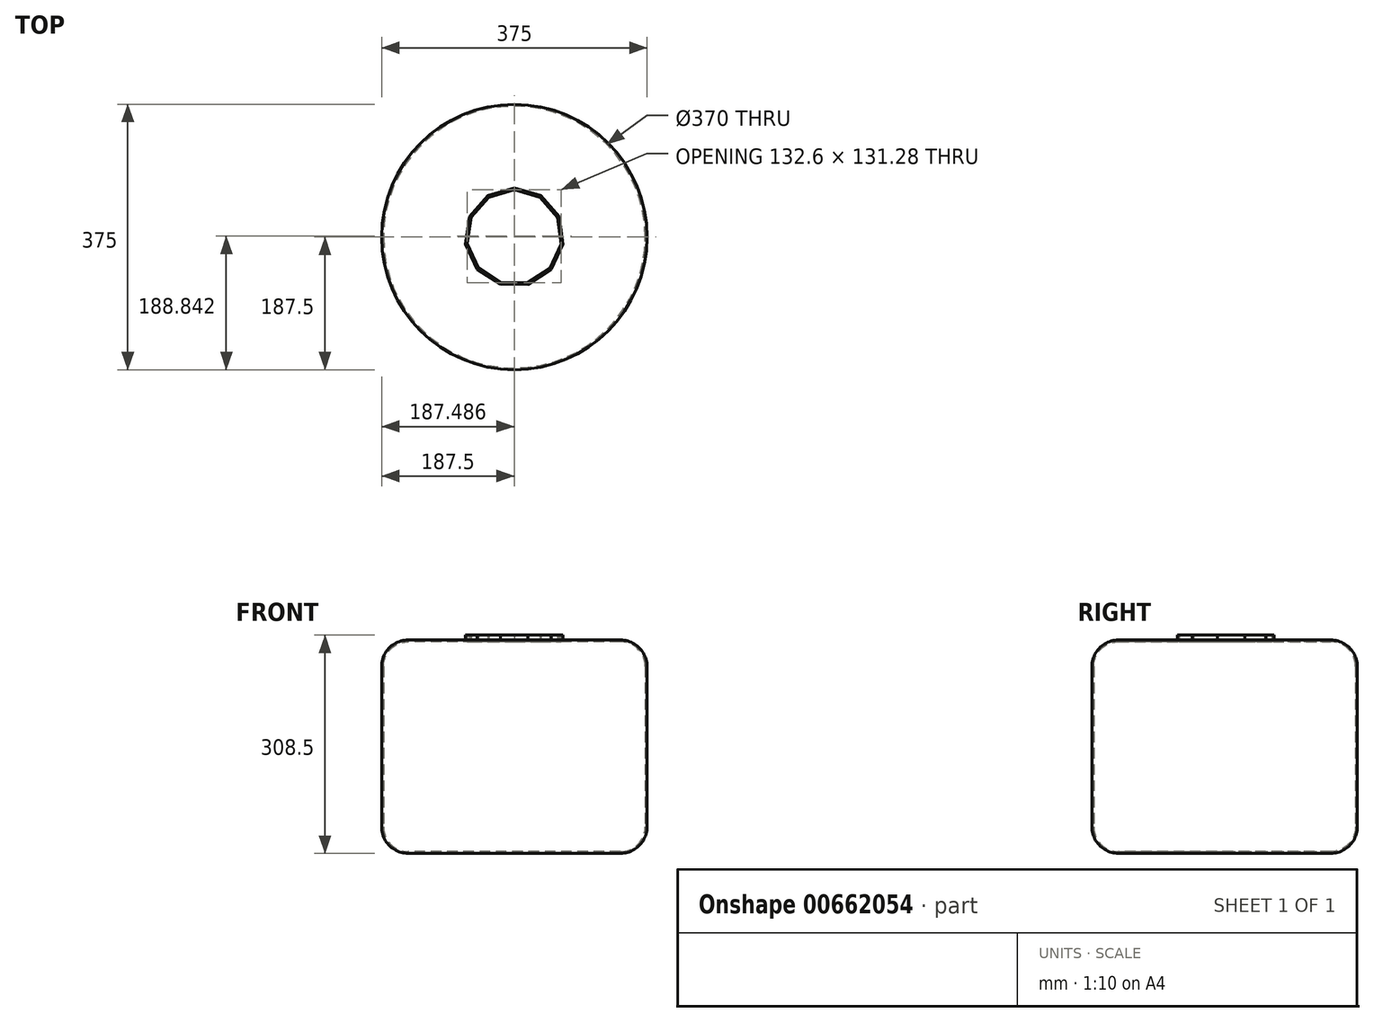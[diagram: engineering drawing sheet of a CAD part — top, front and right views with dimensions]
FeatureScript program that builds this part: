
annotation { "Feature Type Name" : "Feature", "Feature Type Description" : "" }
export const myFeature = defineFeature(function(context is Context, id is Id, definition is map)
    precondition{}
    {
        {
            var Q0;
            Q0=qCreatedBy(makeId("Top.planeOp"),FACE);
            var sketch = newSketch(context, id + "F0", { "sketchPlane" : qUnion([Q0])});
            skCircle(sketch, "E0", {"center": v(0, 0) * mm, "radius": 250 * mm});
            skSolve(sketch);
        }
        {
            var Q0;
            Q0=qSketchRegion(id+"F0",true);
            extrude(context, id + "F1", {"entities" : qUnion([Q0]), "depth" : 402 * mm, "offsetDistance" : 25 * mm});
        }
        {
            var Q0;
            Q0=makeQuery(id+"F1.opExtrude","CAP_EDGE",EDGE,{"disambiguationData":[OSD([sQuery(id+"F0.wireOp",EDGE,"E0")])],"isStart":false});
            var Q1;
            Q1=makeQuery(id+"F1.opExtrude","CAP_EDGE",EDGE,{"disambiguationData":[OSD([sQuery(id+"F0.wireOp",EDGE,"E0")])],"isStart":true});
            fillet(context, id + "F2", {"entities" : qUnion([Q0, Q1]), "radius" : 50 * mm, "tangentPropagation" : true, "allowEdgeOverflow" : false});
        }
        {
            var Q0;
            Q0=makeQuery(id+"F1.opExtrude","SWEPT_BODY",BODY,{"disambiguationData":[OSD([sQuery(id+"F0.wireOp",EDGE,"E0")])]});
            var Q1;
            Q1=qCreatedBy(makeId("Origin.pointOp"),VERTEX);
            transform(context, id + "F3", {"entities" : qUnion([Q0]), "transformType" : TransformType.SCALE_UNIFORMLY, "scale" : .75, "scalePoint" : qUnion([Q1]), "makeCopy" : false});
        }
        {
            var Q0;
            Q0=makeQuery(id+"F1.opExtrude","CAP_FACE",FACE,{"disambiguationData":[OSD([sQuery(id+"F0.wireOp",EDGE,"E0")])],"isStart":false});
            var sketch = newSketch(context, id + "F4", { "sketchPlane" : qUnion([Q0])});
            skCircle(sketch, "E1.cCircle", {"center": v(0, 0) * mm, "radius": 66.77 * mm, "construction": true});
            skLineSegment(sketch, "E1.0", {"start": v(68.86, -10) * mm, "end": v(52.52, -45.65) * mm});
            skLineSegment(sketch, "E1.1", {"start": v(52.52, -45.65) * mm, "end": v(19.5, -66.8) * mm});
            skLineSegment(sketch, "E1.2", {"start": v(19.5, -66.8) * mm, "end": v(-19.7, -66.74) * mm});
            skLineSegment(sketch, "E1.3", {"start": v(-19.7, -66.74) * mm, "end": v(-52.66, -45.49) * mm});
            skLineSegment(sketch, "E1.4", {"start": v(-52.66, -45.49) * mm, "end": v(-68.9, -9.8) * mm});
            skLineSegment(sketch, "E1.5", {"start": v(-68.9, -9.8) * mm, "end": v(-63.25, 29) * mm});
            skLineSegment(sketch, "E1.6", {"start": v(-63.25, 29) * mm, "end": v(-37.53, 58.6) * mm});
            skLineSegment(sketch, "E1.7", {"start": v(-37.53, 58.6) * mm, "end": v(0.1, 69.59) * mm});
            skLineSegment(sketch, "E1.8", {"start": v(0.1, 69.59) * mm, "end": v(37.71, 58.48) * mm});
            skLineSegment(sketch, "E1.9", {"start": v(37.71, 58.48) * mm, "end": v(63.34, 28.8) * mm});
            skLineSegment(sketch, "E1.10", {"start": v(63.34, 28.8) * mm, "end": v(68.86, -10) * mm});
            skPoint(sketch, "E1.0.midPoint", {"position": v(60.7, -27.83) * mm});
            skSolve(sketch);
        }
        {
            var Q0;
            Q0=makeQuery(id+"F4.imprint","IMPRINT",FACE,{"disambiguationData":[TD([[makeQuery(id+"F4.imprint","IMPRINT",EDGE,{"derivedFrom":sQuery(id+"F4.wireOp",EDGE,"E1.0")}),-1.0]])]});
            extrude(context, id + "F5", {"entities" : qUnion([Q0]), "operationType" : NewBodyOperationType.ADD, "depth" : 7 * mm, "offsetDistance" : 25 * mm});
        }
        {
            var Q0;
            Q0=makeQuery(id+"F5.opExtrude","CAP_FACE",FACE,{"disambiguationData":[OSD([sQuery(id+"F4.wireOp",EDGE,"E1.0"),sQuery(id+"F4.wireOp",EDGE,"E1.1"),sQuery(id+"F4.wireOp",EDGE,"E1.2"),sQuery(id+"F4.wireOp",EDGE,"E1.3"),sQuery(id+"F4.wireOp",EDGE,"E1.4"),sQuery(id+"F4.wireOp",EDGE,"E1.5"),sQuery(id+"F4.wireOp",EDGE,"E1.6"),sQuery(id+"F4.wireOp",EDGE,"E1.7"),sQuery(id+"F4.wireOp",EDGE,"E1.8"),sQuery(id+"F4.wireOp",EDGE,"E1.9"),sQuery(id+"F4.wireOp",EDGE,"E1.10")])],"isStart":false});
            shell(context, id + "F6", {"entities" : qUnion([Q0]), "thickness" : 2.5 * mm});
        }
    });
